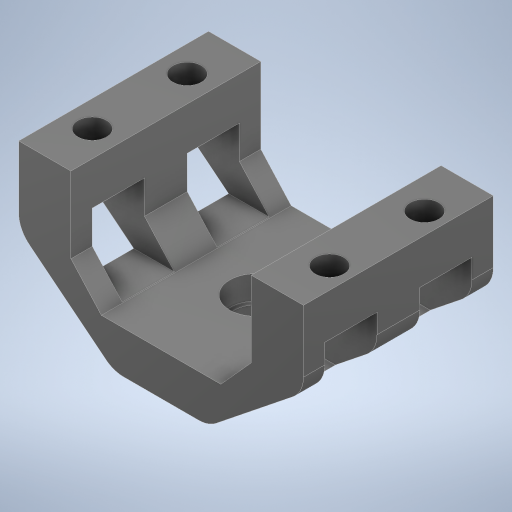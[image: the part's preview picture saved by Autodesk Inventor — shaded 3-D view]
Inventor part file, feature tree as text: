
AUTODESK INVENTOR PART (.ipt)
format: ipt  version: 2024.3 (Build 283343000, 343)  size: 294,400 bytes
history: native  units: in
note: dims shown in document units (in); Inventor stores cm internally (conversion verified against a paired STEP export)
features: extrude x2, sketch x2, other x1
ambient origin geometry x8: Origin, YZ Plane, XZ Plane, XY Plane, X Axis, Y Axis, Z Axis, Center Point
bodies: Solid1 (feature_tree)
feature tree (5):
  extrude  "Extrusion1"  Depth=0.7874in TaperAngle=0.0deg
  extrude  "Extrusion2"  Depth=0.1772in TaperAngle=0.0deg
  sketch  "Sketch1"  dims[d0=0.7874in d2=0.3937in d3=0.7874in d5=0.9843in d8=0.0394in d9=0.0in]
  sketch  "Sketch2"  dims[d10=0.1772in d11=0.1378in d12=0.0in]
  other  "Cortar-Extruir6"
